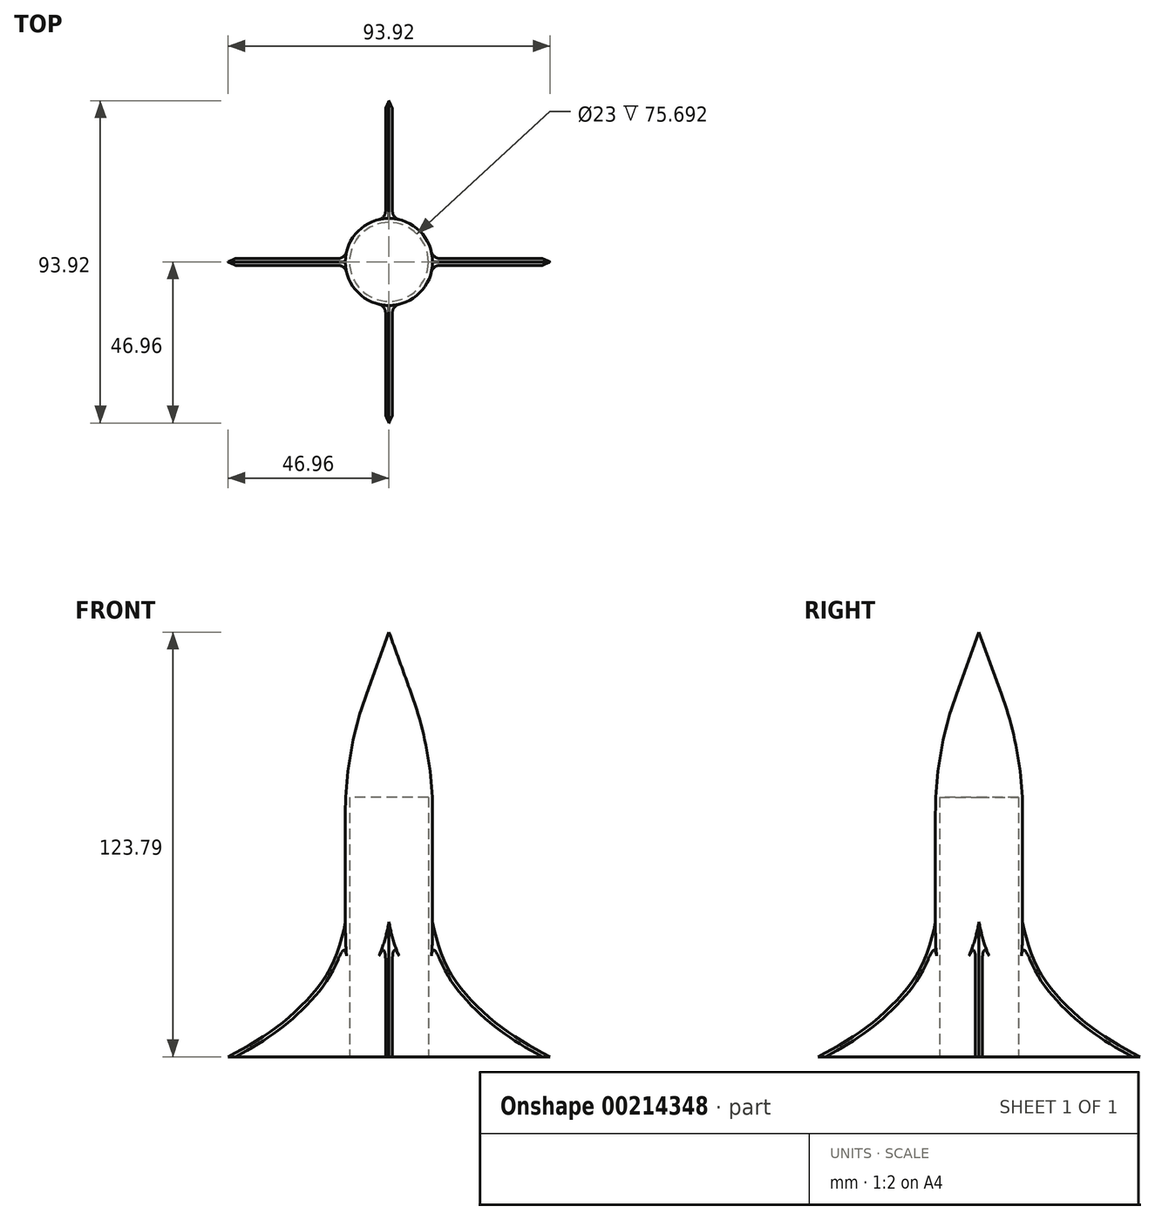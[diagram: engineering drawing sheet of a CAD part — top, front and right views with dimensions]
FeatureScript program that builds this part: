
annotation { "Feature Type Name" : "Feature", "Feature Type Description" : "" }
export const myFeature = defineFeature(function(context is Context, id is Id, definition is map)
    precondition{}
    {
        {
            var Q0;
            Q0=qCreatedBy(makeId("Top.planeOp"),FACE);
            var sketch = newSketch(context, id + "F0", { "sketchPlane" : qUnion([Q0])});
            skCircle(sketch, "E0", {"center": v(0, 0) * mm, "radius": 11.5 * mm});
            skSolve(sketch);
        }
        {
            var Q0;
            Q0=qCreatedBy(makeId("Top.planeOp"),FACE);
            var sketch = newSketch(context, id + "F1", { "sketchPlane" : qUnion([Q0])});
            skCircle(sketch, "E1", {"center": v(0, 0) * mm, "radius": 12.7 * mm});
            skSolve(sketch);
        }
        {
            var Q0;
            Q0=makeQuery(id+"F1.imprint","IMPRINT",FACE,{"disambiguationData":[TD([[makeQuery(id+"F1.imprint","IMPRINT",EDGE,{"derivedFrom":sQuery(id+"F1.wireOp",EDGE,"E1")}),1.0]])]});
            extrude(context, id + "F2", {"entities" : qUnion([Q0]), "depth" : 88.9 * mm});
        }
        {
            var Q0;
            Q0=makeQuery(id+"F2.opExtrude","CAP_FACE",FACE,{"disambiguationData":[OSD([sQuery(id+"F1.wireOp",EDGE,"E1")])],"isStart":false});
            extrude(context, id + "F3", {"entities" : qUnion([Q0]), "operationType" : NewBodyOperationType.ADD, "depth" : 38.1 * mm, "hasDraft" : true, "draftAngle" : 20 * degree, "draftPullDirection" : true});
        }
        {
            var Q0;
            Q0=qCreatedBy(makeId("Front.planeOp"),FACE);
            var sketch = newSketch(context, id + "F4", { "sketchPlane" : qUnion([Q0])});
            skFitSpline(sketch, "E2", {"points": [v(-12.15, 47.73) * mm, v(-25.74, 15.4) * mm, v(-48.14, 0) * mm], "startDerivative": vector(-7.88, -101.44) * mm, "endDerivative": vector(-64.69, -31.63) * mm});
            skLineSegment(sketch, "E3", {"start": v(-48.14, 0) * mm, "end": v(-11.78, 0) * mm});
            skLineSegment(sketch, "E4", {"start": v(-11.78, 0) * mm, "end": v(-12.15, 47.73) * mm});
            skSolve(sketch);
        }
        {
            var Q0;
            Q0 = qSketchRegion(id + "F4", true);
            extrude(context, id + "F5", {"entities" : qUnion([Q0]), "endBound" : BoundingType.SYMMETRIC, "depth" : 2 * mm});
        }
        {
            var Q0;
            Q0=makeQuery(id+"F5.opExtrude","CAP_EDGE",EDGE,{"disambiguationData":[OSD([sQuery(id+"F4.wireOp",EDGE,"E2")])],"isStart":false});
            var Q1;
            Q1=makeQuery(id+"F5.opExtrude","CAP_EDGE",EDGE,{"disambiguationData":[OSD([sQuery(id+"F4.wireOp",EDGE,"E2")])],"isStart":true});
            chamfer(context, id + "F6", {"entities" : qUnion([Q0, Q1]), "width" : 1.52 * mm, "tangentPropagation" : true});
        }
        {
            var Q0;
            Q0=makeQuery(id+"F5.opExtrude","SWEPT_BODY",BODY,{"disambiguationData":[OSD([sQuery(id+"F4.wireOp",EDGE,"E2"),sQuery(id+"F4.wireOp",EDGE,"E3"),sQuery(id+"F4.wireOp",EDGE,"E4")])]});
            var Q1;
            Q1=makeQuery(id+"F2.opExtrude","SWEPT_FACE",FACE,{"disambiguationData":[OSD([sQuery(id+"F1.wireOp",EDGE,"E1")])]});
            circularPattern(context, id + "F7", {"entities" : qUnion([Q0]), "axis" : qUnion([Q1]), "angle" : 360 * degree, "instanceCount" : 4, "equalSpace" : true});
        }
        {
            var Q0;
            {var subQ0=sQuery(id+"F1.wireOp",EDGE,"E1");Q0=makeQuery(id+"F3.boolean.opBoolean","MERGE",EDGE,{"derivedFrom":[makeQuery(id+"F2.opExtrude","CAP_EDGE",EDGE,{"disambiguationData":[OSD([subQ0])],"isStart":false}),makeQuery(id+"F3.opExtrude","CAP_EDGE",EDGE,{"disambiguationData":[OSD([subQ0])],"isStart":true})]});}
            fillet(context, id + "F8", {"entities" : qUnion([Q0]), "radius" : 101.6 * mm, "tangentPropagation" : true, "allowEdgeOverflow" : false});
        }
        {
            var Q0;
            Q0=makeQuery(id+"F2.opExtrude","SWEPT_BODY",BODY,{"disambiguationData":[OSD([sQuery(id+"F1.wireOp",EDGE,"E1")])]});
            var Q1;
            Q1=makeQuery(id+"F7.opPattern","COPY",BODY,{"derivedFrom":makeQuery(id+"F5.opExtrude","SWEPT_BODY",BODY,{"disambiguationData":[OSD([sQuery(id+"F4.wireOp",EDGE,"E2"),sQuery(id+"F4.wireOp",EDGE,"E3"),sQuery(id+"F4.wireOp",EDGE,"E4")])]}),"instanceName":"3"});
            var Q2;
            Q2=makeQuery(id+"F7.opPattern","COPY",BODY,{"derivedFrom":makeQuery(id+"F5.opExtrude","SWEPT_BODY",BODY,{"disambiguationData":[OSD([sQuery(id+"F4.wireOp",EDGE,"E2"),sQuery(id+"F4.wireOp",EDGE,"E3"),sQuery(id+"F4.wireOp",EDGE,"E4")])]}),"instanceName":"2"});
            var Q3;
            Q3=makeQuery(id+"F7.opPattern","COPY",BODY,{"derivedFrom":makeQuery(id+"F5.opExtrude","SWEPT_BODY",BODY,{"disambiguationData":[OSD([sQuery(id+"F4.wireOp",EDGE,"E2"),sQuery(id+"F4.wireOp",EDGE,"E3"),sQuery(id+"F4.wireOp",EDGE,"E4")])]}),"instanceName":"1"});
            var Q4;
            Q4=makeQuery(id+"F5.opExtrude","SWEPT_BODY",BODY,{"disambiguationData":[OSD([sQuery(id+"F4.wireOp",EDGE,"E2"),sQuery(id+"F4.wireOp",EDGE,"E3"),sQuery(id+"F4.wireOp",EDGE,"E4")])]});
            booleanBodies(context, id + "F9", {"operationType" : BooleanOperationType.UNION, "tools" : qUnion([Q0, Q1, Q2, Q3, Q4])});
        }
        {
            var Q0;
            Q0=makeQuery(id+"F9.opBoolean","INTERSECT",EDGE,{"derivedFrom":[makeQuery(id+"F7.opPattern","COPY",FACE,{"derivedFrom":makeQuery(id+"F5.opExtrude","CAP_FACE",FACE,{"disambiguationData":[OSD([sQuery(id+"F4.wireOp",EDGE,"E2"),sQuery(id+"F4.wireOp",EDGE,"E3"),sQuery(id+"F4.wireOp",EDGE,"E4")])],"isStart":false}),"instanceName":"2"}),makeQuery(id+"F2.opExtrude","SWEPT_FACE",FACE,{"disambiguationData":[OSD([sQuery(id+"F1.wireOp",EDGE,"E1")])]})]});
            var Q1;
            Q1=makeQuery(id+"F9.opBoolean","INTERSECT",EDGE,{"derivedFrom":[makeQuery(id+"F7.opPattern","COPY",FACE,{"derivedFrom":makeQuery(id+"F5.opExtrude","CAP_FACE",FACE,{"disambiguationData":[OSD([sQuery(id+"F4.wireOp",EDGE,"E2"),sQuery(id+"F4.wireOp",EDGE,"E3"),sQuery(id+"F4.wireOp",EDGE,"E4")])],"isStart":true}),"instanceName":"1"}),makeQuery(id+"F2.opExtrude","SWEPT_FACE",FACE,{"disambiguationData":[OSD([sQuery(id+"F1.wireOp",EDGE,"E1")])]})]});
            var Q2;
            Q2=makeQuery(id+"F9.opBoolean","INTERSECT",EDGE,{"derivedFrom":[makeQuery(id+"F7.opPattern","COPY",FACE,{"derivedFrom":makeQuery(id+"F5.opExtrude","CAP_FACE",FACE,{"disambiguationData":[OSD([sQuery(id+"F4.wireOp",EDGE,"E2"),sQuery(id+"F4.wireOp",EDGE,"E3"),sQuery(id+"F4.wireOp",EDGE,"E4")])],"isStart":false}),"instanceName":"1"}),makeQuery(id+"F2.opExtrude","SWEPT_FACE",FACE,{"disambiguationData":[OSD([sQuery(id+"F1.wireOp",EDGE,"E1")])]})]});
            var Q3;
            Q3=makeQuery(id+"F9.opBoolean","INTERSECT",EDGE,{"derivedFrom":[makeQuery(id+"F5.opExtrude","CAP_FACE",FACE,{"disambiguationData":[OSD([sQuery(id+"F4.wireOp",EDGE,"E2"),sQuery(id+"F4.wireOp",EDGE,"E3"),sQuery(id+"F4.wireOp",EDGE,"E4")])],"isStart":true}),makeQuery(id+"F2.opExtrude","SWEPT_FACE",FACE,{"disambiguationData":[OSD([sQuery(id+"F1.wireOp",EDGE,"E1")])]})]});
            var Q4;
            Q4=makeQuery(id+"F9.opBoolean","INTERSECT",EDGE,{"derivedFrom":[makeQuery(id+"F5.opExtrude","CAP_FACE",FACE,{"disambiguationData":[OSD([sQuery(id+"F4.wireOp",EDGE,"E2"),sQuery(id+"F4.wireOp",EDGE,"E3"),sQuery(id+"F4.wireOp",EDGE,"E4")])],"isStart":false}),makeQuery(id+"F2.opExtrude","SWEPT_FACE",FACE,{"disambiguationData":[OSD([sQuery(id+"F1.wireOp",EDGE,"E1")])]})]});
            var Q5;
            Q5=makeQuery(id+"F9.opBoolean","INTERSECT",EDGE,{"derivedFrom":[makeQuery(id+"F7.opPattern","COPY",FACE,{"derivedFrom":makeQuery(id+"F5.opExtrude","CAP_FACE",FACE,{"disambiguationData":[OSD([sQuery(id+"F4.wireOp",EDGE,"E2"),sQuery(id+"F4.wireOp",EDGE,"E3"),sQuery(id+"F4.wireOp",EDGE,"E4")])],"isStart":true}),"instanceName":"3"}),makeQuery(id+"F2.opExtrude","SWEPT_FACE",FACE,{"disambiguationData":[OSD([sQuery(id+"F1.wireOp",EDGE,"E1")])]})]});
            var Q6;
            Q6=makeQuery(id+"F9.opBoolean","INTERSECT",EDGE,{"derivedFrom":[makeQuery(id+"F7.opPattern","COPY",FACE,{"derivedFrom":makeQuery(id+"F5.opExtrude","CAP_FACE",FACE,{"disambiguationData":[OSD([sQuery(id+"F4.wireOp",EDGE,"E2"),sQuery(id+"F4.wireOp",EDGE,"E3"),sQuery(id+"F4.wireOp",EDGE,"E4")])],"isStart":true}),"instanceName":"2"}),makeQuery(id+"F2.opExtrude","SWEPT_FACE",FACE,{"disambiguationData":[OSD([sQuery(id+"F1.wireOp",EDGE,"E1")])]})]});
            var Q7;
            Q7=makeQuery(id+"F9.opBoolean","INTERSECT",EDGE,{"derivedFrom":[makeQuery(id+"F7.opPattern","COPY",FACE,{"derivedFrom":makeQuery(id+"F5.opExtrude","CAP_FACE",FACE,{"disambiguationData":[OSD([sQuery(id+"F4.wireOp",EDGE,"E2"),sQuery(id+"F4.wireOp",EDGE,"E3"),sQuery(id+"F4.wireOp",EDGE,"E4")])],"isStart":false}),"instanceName":"3"}),makeQuery(id+"F2.opExtrude","SWEPT_FACE",FACE,{"disambiguationData":[OSD([sQuery(id+"F1.wireOp",EDGE,"E1")])]})]});
            fillet(context, id + "F10", {"entities" : qUnion([Q0, Q1, Q2, Q3, Q4, Q5, Q6, Q7]), "radius" : 2.54 * mm, "tangentPropagation" : true, "allowEdgeOverflow" : false});
        }
        {
            var Q0;
            Q0=makeQuery(id+"F0.imprint","IMPRINT",FACE,{"disambiguationData":[TD([[makeQuery(id+"F0.imprint","IMPRINT",EDGE,{"derivedFrom":sQuery(id+"F0.wireOp",EDGE,"E0")}),1.0]])]});
            extrude(context, id + "F11", {"entities" : qUnion([Q0]), "operationType" : NewBodyOperationType.REMOVE, "depth" : 75.7 * mm});
        }
    });
